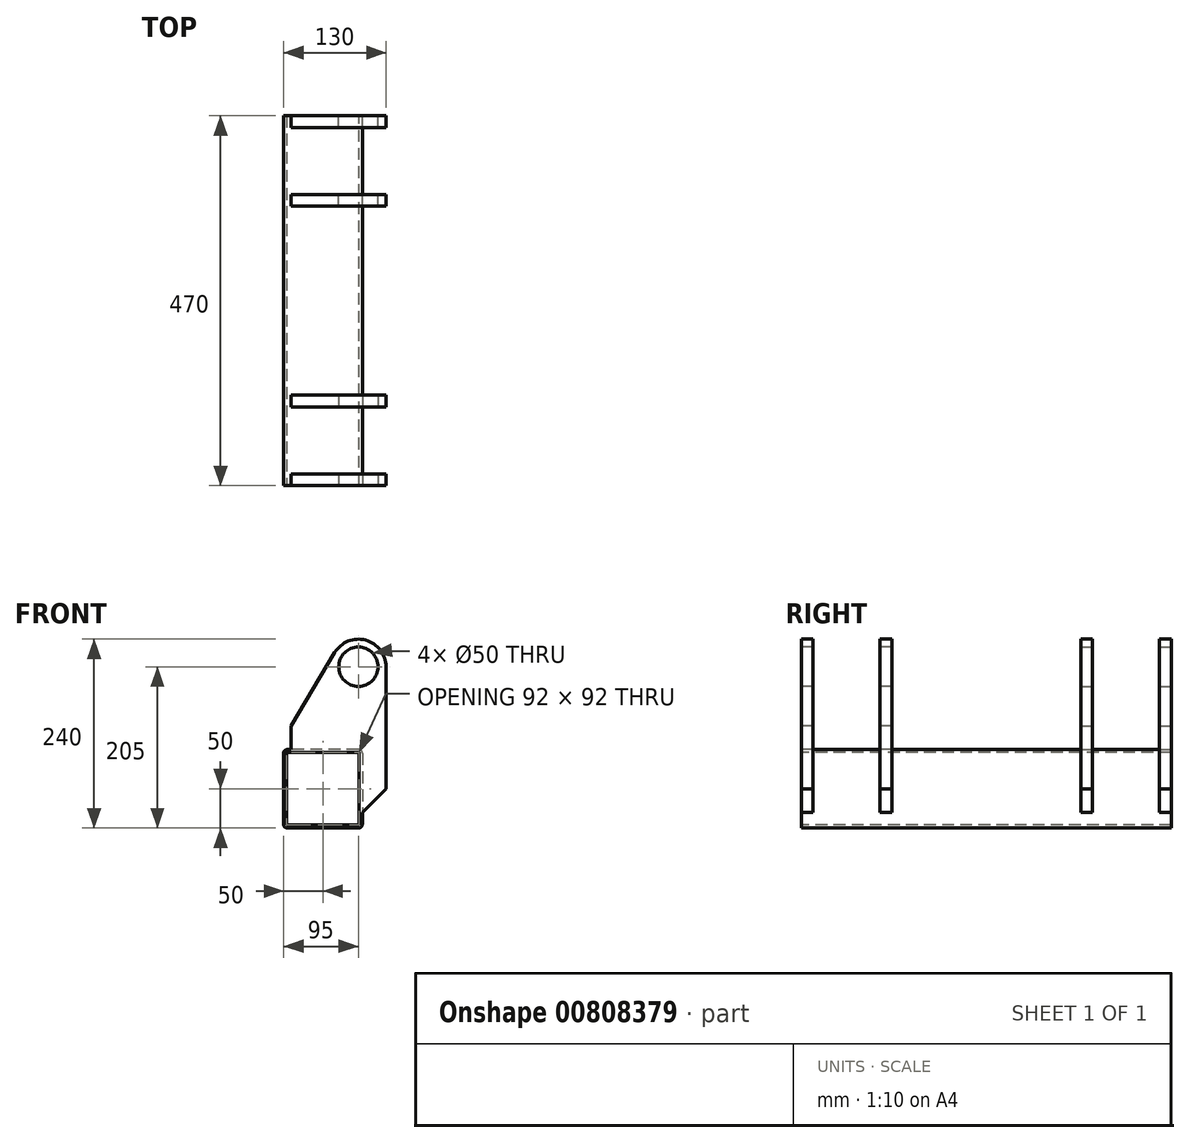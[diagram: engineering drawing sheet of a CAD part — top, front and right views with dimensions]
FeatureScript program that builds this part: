
annotation { "Feature Type Name" : "Feature", "Feature Type Description" : "" }
export const myFeature = defineFeature(function(context is Context, id is Id, definition is map)
    precondition{}
    {
        {
            var Q0;
            Q0=qCreatedBy(makeId("Front.planeOp"),FACE);
            var sketch = newSketch(context, id + "F0", { "sketchPlane" : qUnion([Q0])});
            skLineSegment(sketch, "E0.bottom", {"start": v(45, 50) * mm, "end": v(-45, 50) * mm});
            skLineSegment(sketch, "E0.top", {"start": v(45, -50) * mm, "end": v(-45, -50) * mm});
            skLineSegment(sketch, "E0.left", {"start": v(50, 45) * mm, "end": v(50, -45) * mm});
            skLineSegment(sketch, "E0.right", {"start": v(-50, 45) * mm, "end": v(-50, -45) * mm});
            skPoint(sketch, "E0.middle", {"position": v(0, 0) * mm});
            skPoint(sketch, "E1.visualSharp", {"position": v(-50, 50) * mm});
            skArc(sketch, "E1.filletArc", {"start": v(-45, 50) * mm, "mid": v(-48.54, 48.54) * mm, "end": v(-50, 45) * mm});
            skPoint(sketch, "E2.visualSharp", {"position": v(50, 50) * mm});
            skArc(sketch, "E2.filletArc", {"start": v(50, 45) * mm, "mid": v(48.54, 48.54) * mm, "end": v(45, 50) * mm});
            skPoint(sketch, "E3.visualSharp", {"position": v(50, -50) * mm});
            skArc(sketch, "E3.filletArc", {"start": v(45, -50) * mm, "mid": v(48.54, -48.54) * mm, "end": v(50, -45) * mm});
            skPoint(sketch, "E4.visualSharp", {"position": v(-50, -50) * mm});
            skArc(sketch, "E4.filletArc", {"start": v(-50, -45) * mm, "mid": v(-48.54, -48.54) * mm, "end": v(-45, -50) * mm});
            skLineSegment(sketch, "E5", {"start": v(80, 0) * mm, "end": v(80, 155) * mm});
            skLineSegment(sketch, "E6", {"start": v(-40.38, 80) * mm, "end": v(-40.38, 50) * mm});
            skArc(sketch, "E7", {"start": v(80, 155) * mm, "mid": v(54.28, 188.75) * mm, "end": v(14.93, 172.9) * mm});
            skPoint(sketch, "E8.orphan", {"position": v(80, 190) * mm});
            skLineSegment(sketch, "E9", {"start": v(-40.38, 80) * mm, "end": v(14.93, 172.9) * mm});
            skPoint(sketch, "E10", {"position": v(80, 0) * mm});
            skLineSegment(sketch, "E11", {"start": v(80, 0) * mm, "end": v(50, -30) * mm});
            skCircle(sketch, "E12", {"center": v(45, 155) * mm, "radius": 25 * mm});
            skSolve(sketch);
        }
        {
            var Q0;
            Q0=makeQuery(id+"F0.imprint","IMPRINT",FACE,{"disambiguationData":[TD([[makeQuery(id+"F0.imprint","IMPRINT",EDGE,{"derivedFrom":sQuery(id+"F0.wireOp",EDGE,"E0.bottom")}),1.0]])]});
            extrude(context, id + "F1", {"entities" : qUnion([Q0]), "oppositeDirection" : true, "depth" : 235 * mm, "offsetDistance" : 25 * mm});
        }
        {
            var Q0;
            Q0=makeQuery(id+"F1.opExtrude","CAP_FACE",FACE,{"disambiguationData":[OSD([sQuery(id+"F0.wireOp",EDGE,"E0.bottom"),sQuery(id+"F0.wireOp",EDGE,"E0.top"),sQuery(id+"F0.wireOp",EDGE,"E0.left"),sQuery(id+"F0.wireOp",EDGE,"E0.right"),sQuery(id+"F0.wireOp",EDGE,"E1.filletArc"),sQuery(id+"F0.wireOp",EDGE,"E2.filletArc"),sQuery(id+"F0.wireOp",EDGE,"E3.filletArc"),sQuery(id+"F0.wireOp",EDGE,"E4.filletArc")])],"isStart":true});
            var Q1;
            Q1=makeQuery(id+"F1.opExtrude","CAP_FACE",FACE,{"disambiguationData":[OSD([sQuery(id+"F0.wireOp",EDGE,"E0.bottom"),sQuery(id+"F0.wireOp",EDGE,"E0.top"),sQuery(id+"F0.wireOp",EDGE,"E0.left"),sQuery(id+"F0.wireOp",EDGE,"E0.right"),sQuery(id+"F0.wireOp",EDGE,"E1.filletArc"),sQuery(id+"F0.wireOp",EDGE,"E2.filletArc"),sQuery(id+"F0.wireOp",EDGE,"E3.filletArc"),sQuery(id+"F0.wireOp",EDGE,"E4.filletArc")])],"isStart":false});
            shell(context, id + "F2", {"entities" : qUnion([Q0, Q1]), "thickness" : 4 * mm});
        }
        {
            var Q0;
            {var subQ0=sQuery(id+"F0.wireOp",EDGE,"E2.filletArc");Q0=makeQuery(id+"F0.imprint","IMPRINT",FACE,{"disambiguationData":[TD([[makeQuery(id+"F0.imprint","IMPRINT",EDGE,{"derivedFrom":subQ0}),-1.0]])]});}
            extrude(context, id + "F3", {"entities" : qUnion([Q0]), "oppositeDirection" : true, "depth" : 15 * mm, "offsetDistance" : 25 * mm});
        }
        {
            var Q0;
            Q0=makeQuery(id+"F3.opExtrude","SWEPT_BODY",BODY,{"disambiguationData":[OSD([sQuery(id+"F0.wireOp",EDGE,"E0.bottom"),sQuery(id+"F0.wireOp",EDGE,"E0.left"),sQuery(id+"F0.wireOp",EDGE,"E2.filletArc"),sQuery(id+"F0.wireOp",EDGE,"E5"),sQuery(id+"F0.wireOp",EDGE,"E6"),sQuery(id+"F0.wireOp",EDGE,"E7"),sQuery(id+"F0.wireOp",EDGE,"E9"),sQuery(id+"F0.wireOp",EDGE,"E11"),sQuery(id+"F0.wireOp",EDGE,"E12")])]});
            var Q1;
            Q1=makeQuery(id+"F3.opExtrude","CAP_FACE",FACE,{"disambiguationData":[OSD([sQuery(id+"F0.wireOp",EDGE,"E0.bottom"),sQuery(id+"F0.wireOp",EDGE,"E0.left"),sQuery(id+"F0.wireOp",EDGE,"E2.filletArc"),sQuery(id+"F0.wireOp",EDGE,"E5"),sQuery(id+"F0.wireOp",EDGE,"E6"),sQuery(id+"F0.wireOp",EDGE,"E7"),sQuery(id+"F0.wireOp",EDGE,"E9"),sQuery(id+"F0.wireOp",EDGE,"E11"),sQuery(id+"F0.wireOp",EDGE,"E12")])],"isStart":false});
            transform(context, id + "F4", {"entities" : qUnion([Q0]), "transformType" : TransformType.TRANSLATION_DISTANCE, "transformDirection" : qUnion([Q1]), "distance" : 100 * mm, "makeCopy" : true});
        }
        {
            var Q0;
            Q0=makeQuery(id+"F1.opExtrude","SWEPT_BODY",BODY,{"disambiguationData":[OSD([sQuery(id+"F0.wireOp",EDGE,"E0.bottom"),sQuery(id+"F0.wireOp",EDGE,"E0.top"),sQuery(id+"F0.wireOp",EDGE,"E0.left"),sQuery(id+"F0.wireOp",EDGE,"E0.right"),sQuery(id+"F0.wireOp",EDGE,"E1.filletArc"),sQuery(id+"F0.wireOp",EDGE,"E2.filletArc"),sQuery(id+"F0.wireOp",EDGE,"E3.filletArc"),sQuery(id+"F0.wireOp",EDGE,"E4.filletArc")])]});
            var Q1;
            Q1=makeQuery(id+"F3.opExtrude","SWEPT_BODY",BODY,{"disambiguationData":[OSD([sQuery(id+"F0.wireOp",EDGE,"E0.bottom"),sQuery(id+"F0.wireOp",EDGE,"E0.left"),sQuery(id+"F0.wireOp",EDGE,"E2.filletArc"),sQuery(id+"F0.wireOp",EDGE,"E5"),sQuery(id+"F0.wireOp",EDGE,"E6"),sQuery(id+"F0.wireOp",EDGE,"E7"),sQuery(id+"F0.wireOp",EDGE,"E9"),sQuery(id+"F0.wireOp",EDGE,"E11"),sQuery(id+"F0.wireOp",EDGE,"E12")])]});
            var Q2;
            Q2=makeQuery(id+"F4.opPattern","COPY",BODY,{"derivedFrom":makeQuery(id+"F3.opExtrude","SWEPT_BODY",BODY,{"disambiguationData":[OSD([sQuery(id+"F0.wireOp",EDGE,"E0.bottom"),sQuery(id+"F0.wireOp",EDGE,"E0.left"),sQuery(id+"F0.wireOp",EDGE,"E2.filletArc"),sQuery(id+"F0.wireOp",EDGE,"E5"),sQuery(id+"F0.wireOp",EDGE,"E6"),sQuery(id+"F0.wireOp",EDGE,"E7"),sQuery(id+"F0.wireOp",EDGE,"E9"),sQuery(id+"F0.wireOp",EDGE,"E11"),sQuery(id+"F0.wireOp",EDGE,"E12")])]}),"instanceName":"1"});
            var Q3;
            Q3=makeQuery(id+"F1.opExtrude","CAP_FACE",FACE,{"disambiguationData":[OSD([sQuery(id+"F0.wireOp",EDGE,"E0.bottom"),sQuery(id+"F0.wireOp",EDGE,"E0.top"),sQuery(id+"F0.wireOp",EDGE,"E0.left"),sQuery(id+"F0.wireOp",EDGE,"E0.right"),sQuery(id+"F0.wireOp",EDGE,"E1.filletArc"),sQuery(id+"F0.wireOp",EDGE,"E2.filletArc"),sQuery(id+"F0.wireOp",EDGE,"E3.filletArc"),sQuery(id+"F0.wireOp",EDGE,"E4.filletArc")])],"isStart":false});
            mirror(context, id + "F5", {"operationType" : NewBodyOperationType.ADD, "entities" : qUnion([Q0, Q1, Q2]), "mirrorPlane" : qUnion([Q3])});
        }
    });
